# Revit family: Lighting Fixture_THE LUCY_busSTRUT_BR-LUCY-U-359-30-U-(F)-(OC)
name_source: partatom
category: Lighting Fixtures
units: mm (PartAtom-declared; Revit-internal decimal feet)

## family parameters
Always vertical = Yes
Cut with Voids When Loaded = No
Light Source = Yes
Maintain Annotation Orientation = No
OmniClass Number = 23.80.70.00
OmniClass Title = Lighting
Part Type = Normal
Room Calculation Point = No
Round Connector Dimension = Use Diameter
Shared = No
Work Plane-Based = No

## types (1)
- BR-LUCY-U-359-30-U-(F)-(OC)
    Ampacity = 20 A
    Apparent Load = 30 VA
    Color Filter = 16777215
    Default Elevation = 0' - 0"
    Dimming Lamp Color Temperature Shift = <None>
    Lamp = LED
    Light Material = Lens BS
    Manufacturer = busSTRUT
    Model = BR-LUCY-U-359-30-U-(F)-(OC)
    Photometric Web File = BR-LUCY-U-359-30-U-(F).IES
    Rated Voltage = 277 V
    Tilt Angle = 90.00°
    Type Comments = LIGHTING FIXTUTE
    URL = https://busstrut.com
    Wattage Comments = 30

## geometry (parser evidence)
native form markers: Sweep x2
no freeform markers — native parametric forms only
